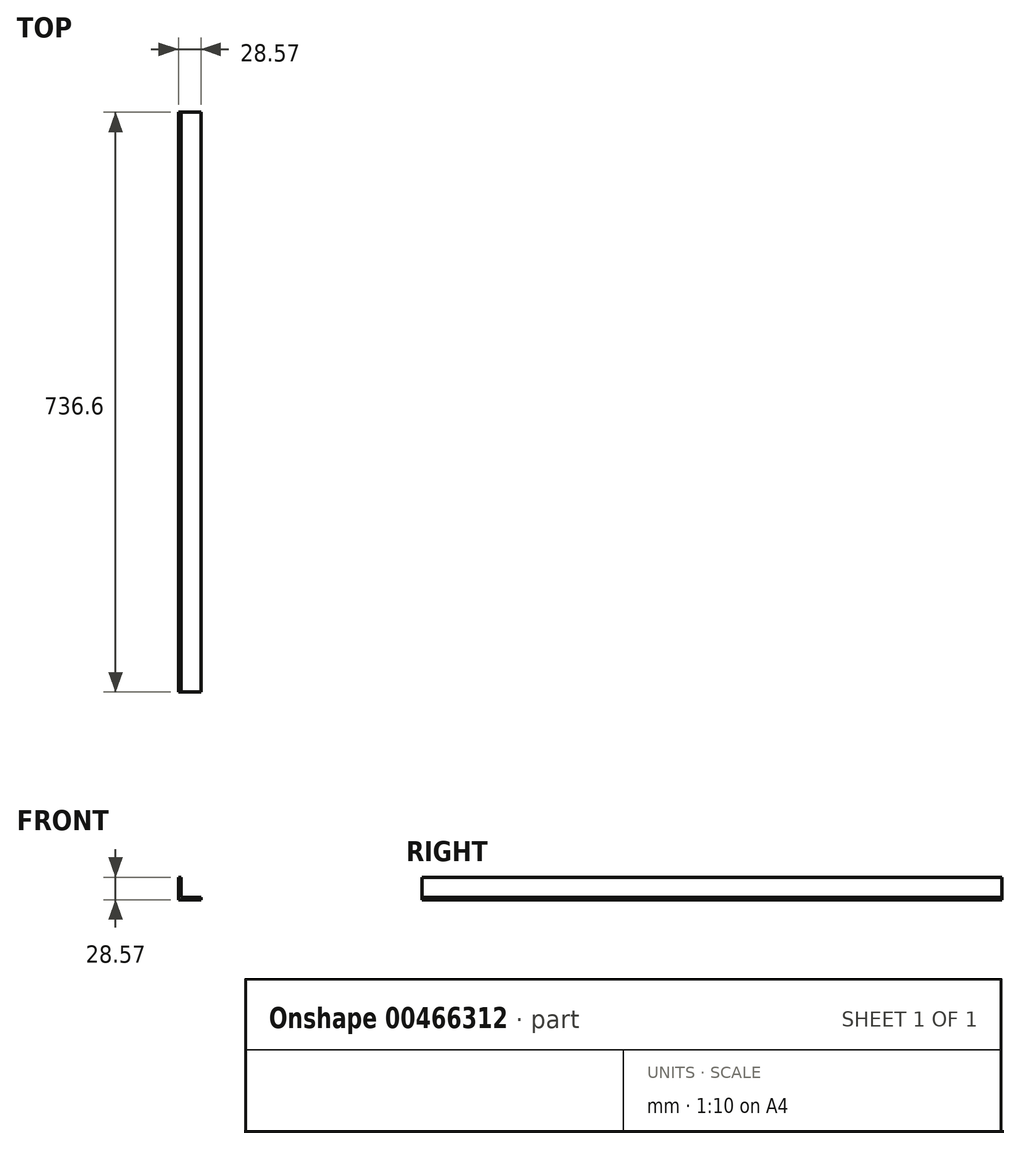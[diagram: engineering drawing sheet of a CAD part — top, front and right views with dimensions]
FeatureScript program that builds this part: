
annotation { "Feature Type Name" : "Feature", "Feature Type Description" : "" }
export const myFeature = defineFeature(function(context is Context, id is Id, definition is map)
    precondition{}
    {
        {
            var Q0;
            Q0=qCreatedBy(makeId("Front.planeOp"),FACE);
            var sketch = newSketch(context, id + "F0", { "sketchPlane" : qUnion([Q0])});
            skLineSegment(sketch, "E0", {"start": v(-25.4, -17.46) * mm, "end": v(0, -17.46) * mm});
            skLineSegment(sketch, "E1", {"start": v(-25.4, -17.46) * mm, "end": v(-25.4, 7.94) * mm});
            skLineSegment(sketch, "E2", {"start": v(-25.4, 7.94) * mm, "end": v(-28.58, 7.94) * mm});
            skLineSegment(sketch, "E3", {"start": v(-28.57, 7.94) * mm, "end": v(-28.57, -20.63) * mm});
            skLineSegment(sketch, "E4", {"start": v(0, -17.46) * mm, "end": v(0, -20.63) * mm});
            skLineSegment(sketch, "E5", {"start": v(0, -20.63) * mm, "end": v(-28.58, -20.63) * mm});
            skSolve(sketch);
        }
        {
            var Q0;
            Q0=qSketchRegion(id+"F0",true);
            extrude(context, id + "F1", {"entities" : qUnion([Q0]), "depth" : 736.6 * mm});
        }
    });
